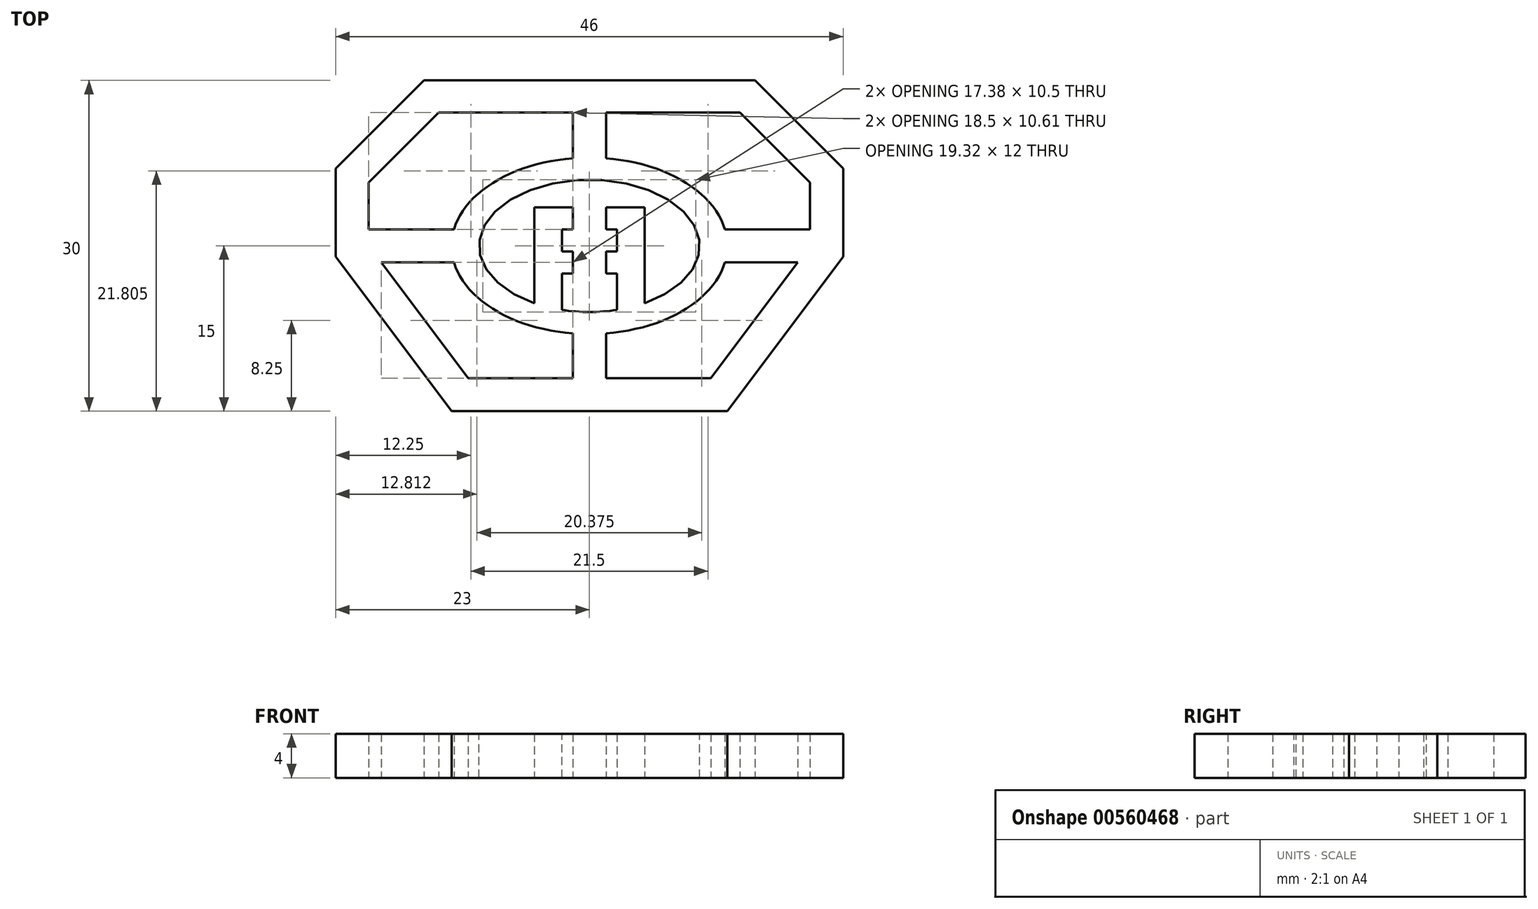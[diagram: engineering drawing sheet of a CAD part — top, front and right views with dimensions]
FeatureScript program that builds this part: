
annotation { "Feature Type Name" : "Feature", "Feature Type Description" : "" }
export const myFeature = defineFeature(function(context is Context, id is Id, definition is map)
    precondition{}
    {
        {
            var Q0;
            Q0=qCreatedBy(makeId("Top.planeOp"),FACE);
            var sketch = newSketch(context, id + "F0", { "sketchPlane" : qUnion([Q0])});
            skLineSegment(sketch, "E0.bottom", {"start": v(15, 15) * mm, "end": v(-15, 15) * mm});
            skLineSegment(sketch, "E0.top", {"start": v(12.5, -15) * mm, "end": v(-12.5, -15) * mm});
            skPoint(sketch, "E0.middle", {"position": v(0, 0) * mm});
            skPoint(sketch, "E1", {"position": v(0, -15) * mm});
            skPoint(sketch, "E2", {"position": v(-12.5, -15) * mm});
            skPoint(sketch, "E3", {"position": v(12.5, -15) * mm});
            skLineSegment(sketch, "E4", {"start": v(-15, 15) * mm, "end": v(-23, 7) * mm});
            skLineSegment(sketch, "E5", {"start": v(15, 15) * mm, "end": v(23, 7) * mm});
            skLineSegment(sketch, "E6", {"start": v(23, 7) * mm, "end": v(23, -1) * mm});
            skLineSegment(sketch, "E7", {"start": v(-23, 7) * mm, "end": v(-23, -1) * mm});
            skLineSegment(sketch, "E8", {"start": v(-23, -1) * mm, "end": v(-12.5, -15) * mm});
            skLineSegment(sketch, "E9", {"start": v(12.5, -15) * mm, "end": v(23, -1) * mm});
            skPoint(sketch, "E10.orphan", {"position": v(-15, -15) * mm});
            skEllipticalArc(sketch, "E11", {});
            skEllipticalArc(sketch, "E12", {});
            skLineSegment(sketch, "E13", {"start": v(13.65, 12.1) * mm, "end": v(1.5, 12.1) * mm});
            skLineSegment(sketch, "E14", {"start": v(11, -12) * mm, "end": v(1.5, -12) * mm});
            skLineSegment(sketch, "E15", {"start": v(20, 5.76) * mm, "end": v(20, 1.5) * mm});
            skLineSegment(sketch, "E16", {"start": v(-11, -12) * mm, "end": v(-18.88, -1.5) * mm});
            skLineSegment(sketch, "E17", {"start": v(-20, 5.76) * mm, "end": v(-20, 1.5) * mm});
            skLineSegment(sketch, "E18", {"start": v(-13.65, 12.1) * mm, "end": v(-20, 5.76) * mm});
            skLineSegment(sketch, "E19.trimOffspring", {"start": v(20, 5.76) * mm, "end": v(13.65, 12.1) * mm});
            skLineSegment(sketch, "E20.trimOffspring", {"start": v(11, -12) * mm, "end": v(18.88, -1.5) * mm});
            skPoint(sketch, "E21", {"position": v(0, 12.1) * mm});
            skPoint(sketch, "E22", {"position": v(0, -12) * mm});
            skPoint(sketch, "E23", {"position": v(-12.5, 0) * mm});
            skPoint(sketch, "E24", {"position": v(12.5, 0) * mm});
            skLineSegment(sketch, "E25", {"start": v(1.5, 12.1) * mm, "end": v(1.5, 7.94) * mm});
            skLineSegment(sketch, "E26.trimOffspring", {"start": v(1.5, -7.94) * mm, "end": v(1.5, -12) * mm});
            skLineSegment(sketch, "E27", {"start": v(-1.5, 12.1) * mm, "end": v(-1.5, 7.94) * mm});
            skLineSegment(sketch, "E28.trimOffspring", {"start": v(-1.5, -7.94) * mm, "end": v(-1.5, -12) * mm});
            skLineSegment(sketch, "E29", {"start": v(-20, 1.5) * mm, "end": v(-12.28, 1.5) * mm});
            skLineSegment(sketch, "E30", {"start": v(-18.88, -1.5) * mm, "end": v(-12.28, -1.5) * mm});
            skLineSegment(sketch, "E31.trimOffspring", {"start": v(12.28, -1.5) * mm, "end": v(18.88, -1.5) * mm});
            skLineSegment(sketch, "E32.trimOffspring", {"start": v(12.28, 1.5) * mm, "end": v(20, 1.5) * mm});
            skLineSegment(sketch, "E33.trimOffspring", {"start": v(-2.5, 1.5) * mm, "end": v(-1.5, 1.5) * mm});
            skPoint(sketch, "E34", {"position": v(0, 1.5) * mm});
            skLineSegment(sketch, "E35", {"start": v(-5, 1.5) * mm, "end": v(-5, -5.2) * mm});
            skLineSegment(sketch, "E36", {"start": v(5, 1.5) * mm, "end": v(5, -5.2) * mm});
            skPoint(sketch, "E37.orphan", {"position": v(-9.68, 1.5) * mm});
            skPoint(sketch, "E38.orphan", {"position": v(9.68, 1.5) * mm});
            skLineSegment(sketch, "E39.trimOffspring", {"start": v(1.5, 1.5) * mm, "end": v(2.5, 1.5) * mm});
            skLineSegment(sketch, "E40.trimOffspring", {"start": v(-1.5, -0.5) * mm, "end": v(-1.5, -2.5) * mm});
            skLineSegment(sketch, "E41.trimOffspring", {"start": v(1.5, -0.5) * mm, "end": v(1.5, -2.5) * mm});
            skLineSegment(sketch, "E42", {"start": v(2.5, -0.5) * mm, "end": v(1.5, -0.5) * mm});
            skLineSegment(sketch, "E43", {"start": v(2.5, -2.5) * mm, "end": v(1.5, -2.5) * mm});
            skPoint(sketch, "E44", {"position": v(0, -2.5) * mm});
            skLineSegment(sketch, "E45", {"start": v(-2.5, -2.5) * mm, "end": v(-2.5, -5.8) * mm});
            skLineSegment(sketch, "E46", {"start": v(2.5, -2.5) * mm, "end": v(2.5, -5.8) * mm});
            skLineSegment(sketch, "E47", {"start": v(5, 1.5) * mm, "end": v(5, 3.5) * mm});
            skLineSegment(sketch, "E48", {"start": v(-5, 1.5) * mm, "end": v(-5, 3.5) * mm});
            skLineSegment(sketch, "E49", {"start": v(5, 3.5) * mm, "end": v(1.5, 3.5) * mm});
            skLineSegment(sketch, "E50", {"start": v(-1.5, 1.5) * mm, "end": v(-1.5, 3.5) * mm});
            skLineSegment(sketch, "E51", {"start": v(1.5, 1.5) * mm, "end": v(1.5, 3.5) * mm});
            skLineSegment(sketch, "E52", {"start": v(2.5, -0.5) * mm, "end": v(2.5, 1.5) * mm});
            skLineSegment(sketch, "E53", {"start": v(-2.5, -0.5) * mm, "end": v(-2.5, 1.5) * mm});
            skLineSegment(sketch, "E54.trimOffspring", {"start": v(-1.5, 3.5) * mm, "end": v(-5, 3.5) * mm});
            skLineSegment(sketch, "E55.trimOffspring", {"start": v(-1.5, -0.5) * mm, "end": v(-2.5, -0.5) * mm});
            skLineSegment(sketch, "E56.trimOffspring", {"start": v(-1.5, -2.5) * mm, "end": v(-2.5, -2.5) * mm});
            skPoint(sketch, "E57.orphan", {"position": v(-5, -2.5) * mm});
            skPoint(sketch, "E58.orphan", {"position": v(5, -2.5) * mm});
            skEllipticalArc(sketch, "E59.trimOffspring", {});
            skEllipticalArc(sketch, "E60.trimOffspring", {});
            skEllipticalArc(sketch, "E61.trimOffspring", {});
            skEllipticalArc(sketch, "E62.trimOffspring", {});
            skLineSegment(sketch, "E63.trimOffspring", {"start": v(-1.5, 12.1) * mm, "end": v(-13.65, 12.1) * mm});
            skLineSegment(sketch, "E64.trimOffspring", {"start": v(-1.5, -12) * mm, "end": v(-11, -12) * mm});
            const initialGuessF0  = {"E11": [0, 0, 1, 0, 0.0125, 0.008, 0.1886163861754045, 1.450506444400108], "E12": [0, 0, 1, 0, 0.01, 0.006, 5.235987755982989, 4.188790204786391], "E59.trimOffspring": [0, 0, 1, 0, 0.01, 0.006, 4.459708725242612, 4.9650692355267685], "E60.trimOffspring": [0, 0, 1, 0, 0.0125, 0.008, 1.6910862091896839, 2.952976267414389], "E61.trimOffspring": [0, 0, 1, 0, 0.0125, 0.008, 3.330209039765196, 4.592099097989902], "E62.trimOffspring": [0, 0, 1, 0, 0.0125, 0.008, 4.832678862779479, 6.094568921004184]};
            skSetInitialGuess(sketch, initialGuessF0);
            skSolve(sketch);
        }
        {
            var Q0;
            Q0 = qSketchRegion(id + "F0", true);
            extrude(context, id + "F1", {"entities" : qUnion([Q0]), "depth" : 4 * mm, "offsetDistance" : 25 * mm});
        }
    });
